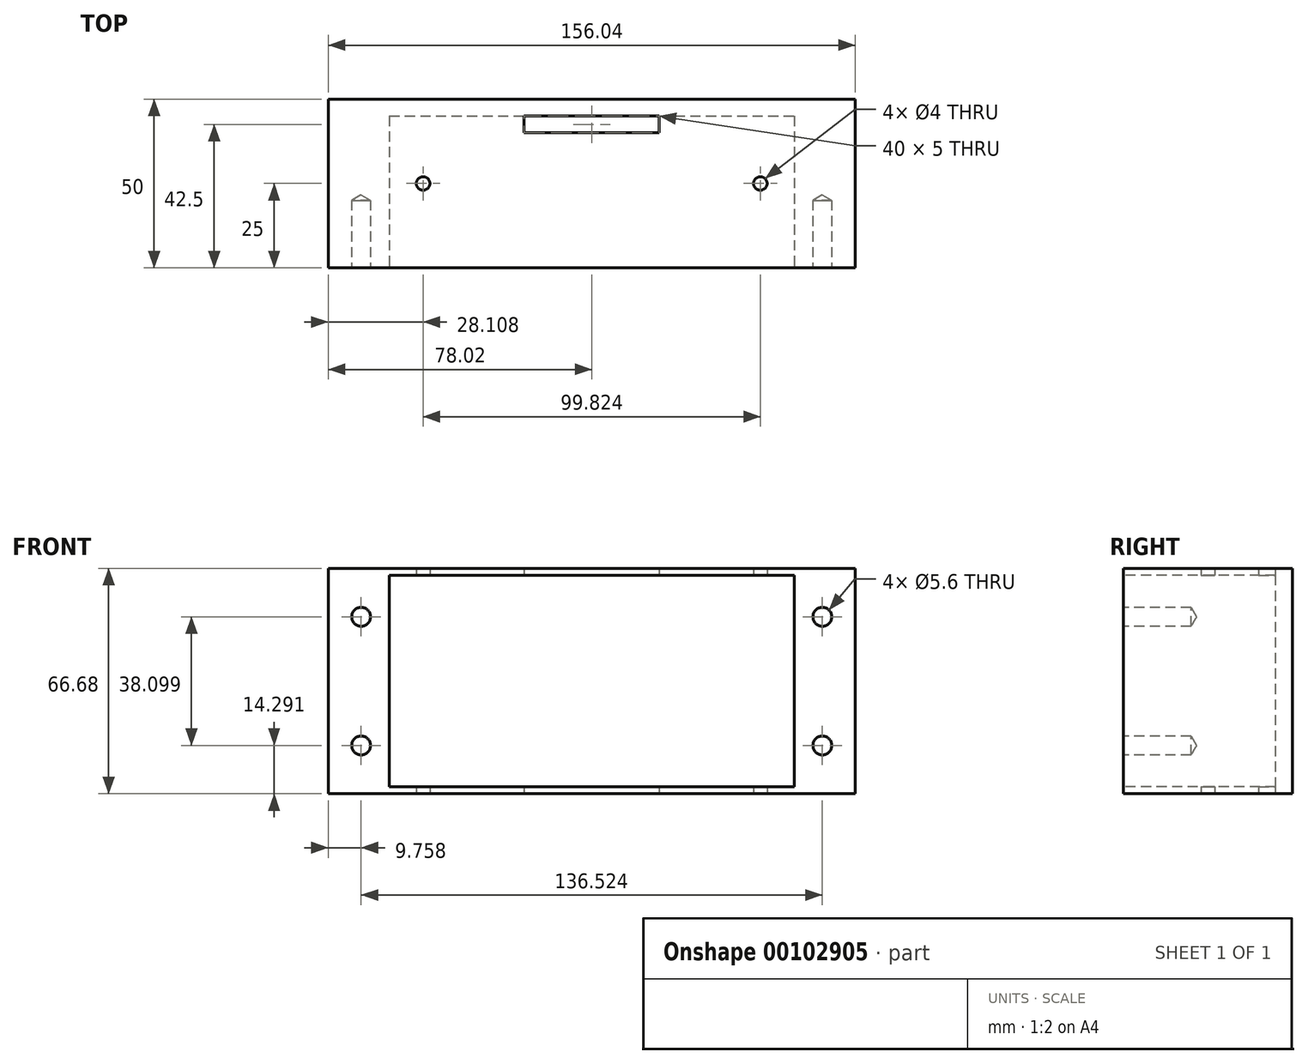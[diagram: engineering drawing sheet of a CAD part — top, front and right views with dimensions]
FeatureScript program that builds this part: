
annotation { "Feature Type Name" : "Feature", "Feature Type Description" : "" }
export const myFeature = defineFeature(function(context is Context, id is Id, definition is map)
    precondition{}
    {
        {
            var Q0;
            Q0=qCreatedBy(makeId("Front.planeOp"),FACE);
            var sketch = newSketch(context, id + "F0", { "sketchPlane" : qUnion([Q0])});
            skLineSegment(sketch, "E0", {"start": v(-68.26, 12.7) * mm, "end": v(-72.23, 12.7) * mm});
            skArc(sketch, "E1", {"start": v(-68.26, -25.4) * mm, "mid": v(-61.91, -19.05) * mm, "end": v(-68.26, -12.7) * mm});
            skArc(sketch, "E2", {"start": v(68.26, -12.7) * mm, "mid": v(61.91, -19.05) * mm, "end": v(68.26, -25.4) * mm});
            skLineSegment(sketch, "E3", {"start": v(72.22, -32.54) * mm, "end": v(72.22, -25.4) * mm});
            skLineSegment(sketch, "E4", {"start": v(-72.23, -32.54) * mm, "end": v(-72.23, -25.4) * mm});
            skLineSegment(sketch, "E5", {"start": v(72.22, -32.54) * mm, "end": v(-72.23, -32.54) * mm});
            skArc(sketch, "E6", {"start": v(68.26, 25.4) * mm, "mid": v(61.91, 19.05) * mm, "end": v(68.26, 12.7) * mm});
            skLineSegment(sketch, "E7", {"start": v(-72.23, 32.54) * mm, "end": v(72.23, 32.54) * mm});
            skLineSegment(sketch, "E8", {"start": v(68.26, 12.7) * mm, "end": v(72.22, 12.7) * mm});
            skLineSegment(sketch, "E9", {"start": v(72.22, 25.4) * mm, "end": v(72.22, 32.54) * mm});
            skLineSegment(sketch, "E10", {"start": v(68.26, 25.4) * mm, "end": v(72.22, 25.4) * mm});
            skLineSegment(sketch, "E11", {"start": v(72.22, -12.7) * mm, "end": v(72.22, 12.7) * mm});
            skLineSegment(sketch, "E12", {"start": v(68.26, -12.7) * mm, "end": v(72.22, -12.7) * mm});
            skLineSegment(sketch, "E13", {"start": v(-68.26, -12.7) * mm, "end": v(-72.23, -12.7) * mm});
            skLineSegment(sketch, "E14", {"start": v(-68.26, -25.4) * mm, "end": v(-72.23, -25.4) * mm});
            skLineSegment(sketch, "E15", {"start": v(68.26, -25.4) * mm, "end": v(72.22, -25.4) * mm});
            skLineSegment(sketch, "E16", {"start": v(-72.23, -12.7) * mm, "end": v(-72.23, 12.7) * mm});
            skArc(sketch, "E17", {"start": v(-68.26, 12.7) * mm, "mid": v(-61.91, 19.05) * mm, "end": v(-68.26, 25.4) * mm});
            skLineSegment(sketch, "E18", {"start": v(-72.23, 25.4) * mm, "end": v(-72.23, 32.54) * mm});
            skLineSegment(sketch, "E19", {"start": v(-68.26, 25.4) * mm, "end": v(-72.23, 25.4) * mm});
            skCircle(sketch, "E20", {"center": v(68.26, 19.05) * mm, "radius": 3.24 * mm});
            skCircle(sketch, "E21", {"center": v(68.26, -19.05) * mm, "radius": 3.24 * mm});
            skLineSegment(sketch, "E22", {"start": v(73.03, -33.34) * mm, "end": v(73.03, 33.34) * mm});
            skLineSegment(sketch, "E23", {"start": v(-73.03, 33.34) * mm, "end": v(73.03, 33.34) * mm});
            skLineSegment(sketch, "E24", {"start": v(-73.03, -33.34) * mm, "end": v(-73.03, 33.34) * mm});
            skLineSegment(sketch, "E25", {"start": v(73.03, -33.34) * mm, "end": v(-73.03, -33.34) * mm});
            skCircle(sketch, "E26", {"center": v(-68.26, -19.05) * mm, "radius": 3.24 * mm});
            skCircle(sketch, "E27", {"center": v(-68.26, 19.05) * mm, "radius": 3.24 * mm});
            skSolve(sketch);
        }
        {
            var Q0;
            Q0=qCreatedBy(makeId("Front.planeOp"),FACE);
            var sketch = newSketch(context, id + "F1", { "sketchPlane" : qUnion([Q0])});
            skLineSegment(sketch, "E28.bottom", {"start": v(-78.03, 33.34) * mm, "end": v(78.03, 33.34) * mm});
            skLineSegment(sketch, "E28.top", {"start": v(-78.03, -33.34) * mm, "end": v(78.03, -33.34) * mm});
            skLineSegment(sketch, "E28.left", {"start": v(-78.03, 33.34) * mm, "end": v(-78.03, -33.34) * mm});
            skLineSegment(sketch, "E28.right", {"start": v(78.03, 33.34) * mm, "end": v(78.03, -33.34) * mm});
            skSolve(sketch);
        }
        {
            var Q0;
            Q0=qSketchRegion(id+"F1",true);
            extrude(context, id + "F2", {"entities" : qUnion([Q0]), "oppositeDirection" : true, "depth" : 50 * mm});
        }
        {
            var Q0;
            Q0=sQuery(id+"F0.wireOp",VERTEX,"E17.center");
            var Q1;
            Q1=sQuery(id+"F0.wireOp",VERTEX,"E1.center");
            var Q2;
            Q2=sQuery(id+"F0.wireOp",VERTEX,"E2.center");
            var Q3;
            Q3=sQuery(id+"F0.wireOp",VERTEX,"E6.center");
            var Q4;
            Q4=makeQuery(id+"F2.opExtrude","SWEPT_BODY",BODY,{"disambiguationData":[OSD([sQuery(id+"F1.wireOp",EDGE,"E28.bottom"),sQuery(id+"F1.wireOp",EDGE,"E28.top"),sQuery(id+"F1.wireOp",EDGE,"E28.left"),sQuery(id+"F1.wireOp",EDGE,"E28.right")])]});
            hole(context, id + "F3", {"style" : HoleStyle.SIMPLE, "endStyle" : HoleEndStyle.BLIND, "holeDiameter" : 5.6 * mm, "holeDepth" : 20 * mm, "locations" : qUnion([Q0, Q1, Q2, Q3]), "scope" : qUnion([Q4])});
        }
        {
            var Q0;
            Q0=makeQuery(id+"F0.imprint","IMPRINT",FACE,{"disambiguationData":[TD([[makeQuery(id+"F0.imprint","IMPRINT",EDGE,{"derivedFrom":sQuery(id+"F0.wireOp",EDGE,"E12")}),1.0]])]});
            var sketch = newSketch(context, id + "F4", { "sketchPlane" : qUnion([Q0])});
            skLineSegment(sketch, "E29.bottom", {"start": v(-59.91, 31.34) * mm, "end": v(59.91, 31.34) * mm});
            skLineSegment(sketch, "E29.top", {"start": v(-59.91, -31.34) * mm, "end": v(59.91, -31.34) * mm});
            skLineSegment(sketch, "E29.left", {"start": v(-59.91, 31.34) * mm, "end": v(-59.91, -31.34) * mm});
            skLineSegment(sketch, "E29.right", {"start": v(59.91, 31.34) * mm, "end": v(59.91, -31.34) * mm});
            skSolve(sketch);
        }
        {
            var Q0;
            Q0=qSketchRegion(id+"F4",true);
            extrude(context, id + "F5", {"entities" : qUnion([Q0]), "operationType" : NewBodyOperationType.REMOVE, "oppositeDirection" : true, "depth" : 45 * mm});
        }
        {
            var Q0;
            Q0=makeQuery(id+"F2.opExtrude","SWEPT_FACE",FACE,{"disambiguationData":[OSD([sQuery(id+"F1.wireOp",EDGE,"E28.top")])]});
            var sketch = newSketch(context, id + "F6", { "sketchPlane" : qUnion([Q0])});
            skLineSegment(sketch, "E30.bottom", {"start": v(20, -40) * mm, "end": v(-20, -40) * mm});
            skLineSegment(sketch, "E30.top", {"start": v(20, -45) * mm, "end": v(-20, -45) * mm});
            skLineSegment(sketch, "E30.left", {"start": v(20, -40) * mm, "end": v(20, -45) * mm});
            skLineSegment(sketch, "E30.right", {"start": v(-20, -40) * mm, "end": v(-20, -45) * mm});
            skPoint(sketch, "E30.middle", {"position": v(0, -42.5) * mm});
            skPoint(sketch, "E30.middle.positionSnap0", {"position": v(0, -50) * mm});
            skPoint(sketch, "E30.centerSnap0", {"position": v(0, -50) * mm});
            skSolve(sketch);
        }
        {
            var Q0;
            Q0=qSketchRegion(id+"F6",true);
            extrude(context, id + "F7", {"entities" : qUnion([Q0]), "operationType" : NewBodyOperationType.REMOVE, "endBound" : BoundingType.THROUGH_ALL, "oppositeDirection" : true, "depth" : 25 * mm});
        }
        {
            var Q0;
            Q0=makeQuery(id+"F2.opExtrude","SWEPT_FACE",FACE,{"disambiguationData":[OSD([sQuery(id+"F1.wireOp",EDGE,"E28.top")])]});
            var sketch = newSketch(context, id + "F8", { "sketchPlane" : qUnion([Q0])});
            skPoint(sketch, "E31", {"position": v(-49.91, -25) * mm});
            skPoint(sketch, "E31.positionSnap0", {"position": v(-78.03, -25) * mm});
            skPoint(sketch, "E32.MirrorP", {"position": v(49.91, -25) * mm});
            skSolve(sketch);
        }
        {
            var Q0;
            Q0=sQuery(id+"F8.wireOp",VERTEX,"E31");
            var Q1;
            Q1=sQuery(id+"F8.wireOp",VERTEX,"E32.MirrorP");
            var Q2;
            Q2=makeQuery(id+"F2.opExtrude","SWEPT_BODY",BODY,{"disambiguationData":[OSD([sQuery(id+"F1.wireOp",EDGE,"E28.bottom"),sQuery(id+"F1.wireOp",EDGE,"E28.top"),sQuery(id+"F1.wireOp",EDGE,"E28.left"),sQuery(id+"F1.wireOp",EDGE,"E28.right")])]});
            hole(context, id + "F9", {"style" : HoleStyle.SIMPLE, "endStyle" : HoleEndStyle.THROUGH, "holeDiameter" : 4 * mm, "locations" : qUnion([Q0, Q1]), "scope" : qUnion([Q2]), "isTappedThrough" : true});
        }
    });
